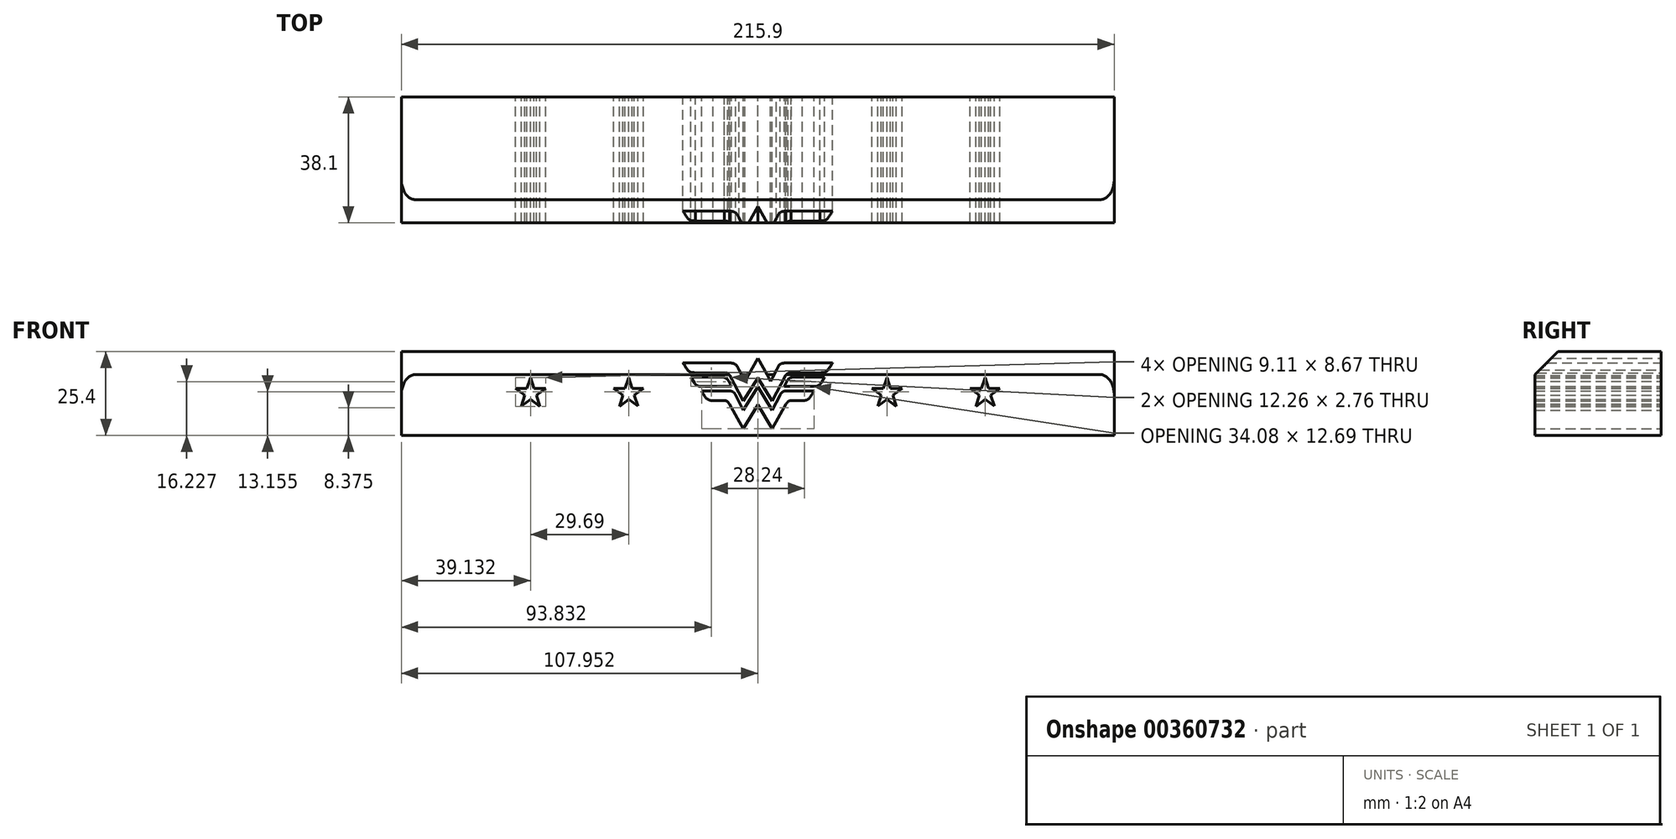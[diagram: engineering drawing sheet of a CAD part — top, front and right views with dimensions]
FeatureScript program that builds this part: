
annotation { "Feature Type Name" : "Feature", "Feature Type Description" : "" }
export const myFeature = defineFeature(function(context is Context, id is Id, definition is map)
    precondition{}
    {
        {
            var Q0;
            Q0=qCreatedBy(makeId("Front.planeOp"),FACE);
            var sketch = newSketch(context, id + "F0", { "sketchPlane" : qUnion([Q0])});
            skLineSegment(sketch, "E0.bottom", {"start": v(-107.29, 21.01) * mm, "end": v(108.61, 21.01) * mm});
            skLineSegment(sketch, "E0.top", {"start": v(-107.29, -4.39) * mm, "end": v(108.61, -4.39) * mm});
            skLineSegment(sketch, "E0.left", {"start": v(-107.29, 21.01) * mm, "end": v(-107.29, -4.39) * mm});
            skLineSegment(sketch, "E0.right", {"start": v(108.61, 21.01) * mm, "end": v(108.61, -4.39) * mm});
            skPoint(sketch, "E1", {"position": v(0.66, 21.01) * mm});
            skLineSegment(sketch, "E2", {"start": v(0.66, 21.01) * mm, "end": v(0.66, -4.39) * mm, "construction": true});
            skPoint(sketch, "E3", {"position": v(-24.74, 21.01) * mm});
            skPoint(sketch, "E4.MirrorP", {"position": v(26.06, 21.01) * mm});
            skLineSegment(sketch, "E5", {"start": v(-24.74, 21.01) * mm, "end": v(-24.74, -4.39) * mm, "construction": true});
            skLineSegment(sketch, "E6", {"start": v(26.06, 21.01) * mm, "end": v(26.06, -4.39) * mm, "construction": true});
            skLineSegment(sketch, "E7", {"start": v(-21.99, 17.6) * mm, "end": v(-8.5, 17.6) * mm});
            skLineSegment(sketch, "E8", {"start": v(-5.01, 15.43) * mm, "end": v(-3.23, 12.05) * mm});
            skLineSegment(sketch, "E9", {"start": v(-3.23, 12.05) * mm, "end": v(0.66, 18.98) * mm});
            skFitSpline(sketch, "E10", {"points": [v(-8.5, 17.6) * mm, v(-5.01, 15.43) * mm], "startDerivative": vector(7.3, -0.1) * mm, "endDerivative": vector(2.43, -5.07) * mm});
            skFitSpline(sketch, "E11", {"points": [v(-21.99, 17.6) * mm, v(-18.2, 14.59) * mm], "startDerivative": vector(5.99, -9.84) * mm, "endDerivative": vector(5.38, -0.2) * mm});
            skLineSegment(sketch, "E12", {"start": v(-18.2, 14.59) * mm, "end": v(-9.4, 14.59) * mm});
            skLineSegment(sketch, "E13", {"start": v(-7.78, 13.77) * mm, "end": v(-3.69, 5.99) * mm});
            skLineSegment(sketch, "E14", {"start": v(-3.69, 5.99) * mm, "end": v(0.66, 13.03) * mm});
            skFitSpline(sketch, "E15", {"points": [v(-9.4, 14.59) * mm, v(-7.78, 13.77) * mm], "startDerivative": vector(2.45, -0.06) * mm, "endDerivative": vector(1.52, -2.05) * mm});
            skLineSegment(sketch, "E16", {"start": v(-19.59, 13.22) * mm, "end": v(-10.08, 13.22) * mm});
            skLineSegment(sketch, "E17", {"start": v(-8.13, 12.02) * mm, "end": v(-7.33, 10.45) * mm});
            skLineSegment(sketch, "E18", {"start": v(-7.33, 10.45) * mm, "end": v(-16.64, 10.45) * mm});
            skLineSegment(sketch, "E19", {"start": v(-18.5, 11.48) * mm, "end": v(-19.59, 13.22) * mm});
            skPoint(sketch, "E20.visualSharp", {"position": v(-17.86, 10.45) * mm});
            skArc(sketch, "E20.filletArc", {"start": v(-18.5, 11.48) * mm, "mid": v(-17.7, 10.73) * mm, "end": v(-16.64, 10.45) * mm});
            skPoint(sketch, "E21.visualSharp", {"position": v(-8.73, 13.22) * mm});
            skArc(sketch, "E21.filletArc", {"start": v(-8.13, 12.02) * mm, "mid": v(-8.93, 12.9) * mm, "end": v(-10.08, 13.22) * mm});
            skLineSegment(sketch, "E22", {"start": v(-16.38, 9.08) * mm, "end": v(-8.11, 9.08) * mm});
            skLineSegment(sketch, "E23", {"start": v(-6.05, 7.77) * mm, "end": v(-3.69, 3.28) * mm});
            skLineSegment(sketch, "E24", {"start": v(-3.69, 3.28) * mm, "end": v(0.66, 10.33) * mm});
            skFitSpline(sketch, "E25", {"points": [v(-16.38, 9.08) * mm, v(-12.85, 6.16) * mm], "startDerivative": vector(4.52, -7.88) * mm, "endDerivative": vector(4.96, -0.07) * mm});
            skLineSegment(sketch, "E26", {"start": v(-12.85, 6.16) * mm, "end": v(-9.48, 6.16) * mm});
            skFitSpline(sketch, "E27", {"points": [v(-9.48, 6.16) * mm, v(-7.94, 5.14) * mm], "startDerivative": vector(2.85, -0.12) * mm, "endDerivative": vector(1.74, -2.2) * mm});
            skLineSegment(sketch, "E28", {"start": v(-7.94, 5.14) * mm, "end": v(-3.69, -2.36) * mm});
            skLineSegment(sketch, "E29", {"start": v(-3.69, -2.36) * mm, "end": v(0.66, 4.88) * mm});
            skLineSegment(sketch, "E30.MirrorCS", {"start": v(4.55, 12.05) * mm, "end": v(0.66, 18.98) * mm});
            skLineSegment(sketch, "E31.MirrorCS", {"start": v(6.33, 15.43) * mm, "end": v(4.55, 12.05) * mm});
            skFitSpline(sketch, "E32.MirrorCS", {"points": [v(9.82, 17.6) * mm, v(6.33, 15.43) * mm], "startDerivative": vector(-7.3, -0.1) * mm, "endDerivative": vector(-2.43, -5.07) * mm});
            skLineSegment(sketch, "E33.MirrorCS", {"start": v(23.31, 17.6) * mm, "end": v(9.82, 17.6) * mm});
            skFitSpline(sketch, "E34.MirrorCS", {"points": [v(23.31, 17.6) * mm, v(19.52, 14.59) * mm], "startDerivative": vector(-5.99, -9.84) * mm, "endDerivative": vector(-5.38, -0.2) * mm});
            skLineSegment(sketch, "E35.MirrorCS", {"start": v(19.52, 14.59) * mm, "end": v(10.73, 14.59) * mm});
            skFitSpline(sketch, "E36.MirrorCS", {"points": [v(10.73, 14.59) * mm, v(9.1, 13.77) * mm], "startDerivative": vector(-2.45, -0.06) * mm, "endDerivative": vector(-1.52, -2.05) * mm});
            skLineSegment(sketch, "E37.MirrorCS", {"start": v(9.1, 13.77) * mm, "end": v(5.01, 5.99) * mm});
            skLineSegment(sketch, "E38.MirrorCS", {"start": v(5.01, 5.99) * mm, "end": v(0.66, 13.03) * mm});
            skLineSegment(sketch, "E39.MirrorCS", {"start": v(20.91, 13.22) * mm, "end": v(11.4, 13.22) * mm});
            skLineSegment(sketch, "E40.MirrorCS", {"start": v(19.82, 11.48) * mm, "end": v(20.91, 13.22) * mm});
            skArc(sketch, "E41.MirrorCS", {"start": v(19.82, 11.48) * mm, "mid": v(19.03, 10.73) * mm, "end": v(17.97, 10.45) * mm});
            skLineSegment(sketch, "E42.MirrorCS", {"start": v(8.65, 10.45) * mm, "end": v(17.97, 10.45) * mm});
            skLineSegment(sketch, "E43.MirrorCS", {"start": v(9.45, 12.02) * mm, "end": v(8.65, 10.45) * mm});
            skArc(sketch, "E44.MirrorCS", {"start": v(9.45, 12.02) * mm, "mid": v(10.26, 12.9) * mm, "end": v(11.4, 13.22) * mm});
            skLineSegment(sketch, "E45.MirrorCS", {"start": v(17.7, 9.08) * mm, "end": v(9.44, 9.08) * mm});
            skLineSegment(sketch, "E46.MirrorCS", {"start": v(7.37, 7.77) * mm, "end": v(5.01, 3.28) * mm});
            skLineSegment(sketch, "E47.MirrorCS", {"start": v(5.01, 3.28) * mm, "end": v(0.66, 10.33) * mm});
            skFitSpline(sketch, "E48.MirrorCS", {"points": [v(17.7, 9.08) * mm, v(14.18, 6.16) * mm], "startDerivative": vector(-4.52, -7.88) * mm, "endDerivative": vector(-4.96, -0.07) * mm});
            skLineSegment(sketch, "E49.MirrorCS", {"start": v(14.18, 6.16) * mm, "end": v(10.8, 6.16) * mm});
            skFitSpline(sketch, "E50.MirrorCS", {"points": [v(10.8, 6.16) * mm, v(9.27, 5.14) * mm], "startDerivative": vector(-2.85, -0.12) * mm, "endDerivative": vector(-1.74, -2.2) * mm});
            skLineSegment(sketch, "E51.MirrorCS", {"start": v(9.27, 5.14) * mm, "end": v(5.01, -2.36) * mm});
            skLineSegment(sketch, "E52.MirrorCS", {"start": v(5.01, -2.36) * mm, "end": v(0.66, 4.88) * mm});
            skFitSpline(sketch, "E53", {"points": [v(-8.11, 9.08) * mm, v(-6.05, 7.77) * mm], "startDerivative": vector(2.51, -0.05) * mm, "endDerivative": vector(1.66, -3.55) * mm});
            skFitSpline(sketch, "E54.MirrorCS", {"points": [v(9.44, 9.08) * mm, v(7.37, 7.77) * mm], "startDerivative": vector(-2.51, -0.05) * mm, "endDerivative": vector(-1.66, -3.55) * mm});
            skSolve(sketch);
        }
        {
            var Q0;
            Q0 = qSketchRegion(id + "F0", true);
            extrude(context, id + "F1", {"entities" : qUnion([Q0]), "depth" : 38.1 * mm, "offsetDistance" : 25.4 * mm});
        }
        {
            var Q0;
            Q0=qCreatedBy(makeId("Front.planeOp"),FACE);
            var sketch = newSketch(context, id + "F2", { "sketchPlane" : qUnion([Q0])});
            skPoint(sketch, "E55.0", {"position": v(0, 0) * mm});
            skPoint(sketch, "E55.1", {"position": v(0.66, 21.01) * mm});
            skPoint(sketch, "E56.0", {"position": v(-107.29, 21.01) * mm});
            skPoint(sketch, "E56.1", {"position": v(108.61, 21.01) * mm});
            skLineSegment(sketch, "E57", {"start": v(-107.29, 21.01) * mm, "end": v(0.66, 21.01) * mm, "construction": true});
            skPoint(sketch, "E58", {"position": v(-53.31, 21.01) * mm});
            skLineSegment(sketch, "E59", {"start": v(0.66, 21.01) * mm, "end": v(108.61, 21.01) * mm, "construction": true});
            skPoint(sketch, "E60", {"position": v(54.64, 21.01) * mm});
            skLineSegment(sketch, "E61", {"start": v(-53.31, 21.01) * mm, "end": v(-53.31, -6.56) * mm, "construction": true});
            skLineSegment(sketch, "E62", {"start": v(54.64, 21.01) * mm, "end": v(54.64, -9.6) * mm, "construction": true});
            skPoint(sketch, "E63.0", {"position": v(-107.29, -4.39) * mm});
            skPoint(sketch, "E63.1", {"position": v(108.61, -4.39) * mm});
            skLineSegment(sketch, "E64", {"start": v(-107.29, 21.01) * mm, "end": v(-107.29, -4.39) * mm, "construction": true});
            skLineSegment(sketch, "E65", {"start": v(108.61, 21.01) * mm, "end": v(108.61, -4.39) * mm, "construction": true});
            skPoint(sketch, "E66", {"position": v(-107.29, 8.31) * mm});
            skPoint(sketch, "E67", {"position": v(108.61, 8.31) * mm});
            skPoint(sketch, "E68.0.midPoint", {"position": v(-34.77, 7.12) * mm});
            skLineSegment(sketch, "E69", {"start": v(-41.27, 4.43) * mm, "end": v(-40.2, 7.74) * mm});
            skLineSegment(sketch, "E70", {"start": v(-38.48, 13.1) * mm, "end": v(-37.4, 9.8) * mm});
            skLineSegment(sketch, "E71", {"start": v(-35.64, 4.44) * mm, "end": v(-38.46, 6.48) * mm});
            skLineSegment(sketch, "E72", {"start": v(-43.02, 9.78) * mm, "end": v(-39.54, 9.79) * mm});
            skLineSegment(sketch, "E73", {"start": v(-33.91, 9.8) * mm, "end": v(-36.72, 7.75) * mm});
            skLineSegment(sketch, "E74.trimOffspring", {"start": v(-36.72, 7.75) * mm, "end": v(-35.64, 4.44) * mm});
            skLineSegment(sketch, "E75.trimOffspring", {"start": v(-37.4, 9.8) * mm, "end": v(-33.91, 9.8) * mm});
            skLineSegment(sketch, "E76.trimOffspring", {"start": v(-39.54, 9.79) * mm, "end": v(-38.48, 13.1) * mm});
            skLineSegment(sketch, "E77.trimOffspring", {"start": v(-40.2, 7.74) * mm, "end": v(-43.02, 9.78) * mm});
            skLineSegment(sketch, "E78.trimOffspring", {"start": v(-38.46, 6.48) * mm, "end": v(-41.27, 4.43) * mm});
            skPoint(sketch, "E68.cCircle.center.orphan", {"position": v(-38.46, 8.31) * mm});
            skLineSegment(sketch, "E79", {"start": v(0.66, 21.01) * mm, "end": v(0.66, -7.13) * mm, "construction": true});
            skLineSegment(sketch, "E80.MirrorCS", {"start": v(38.72, 9.8) * mm, "end": v(35.24, 9.8) * mm});
            skLineSegment(sketch, "E81.MirrorCS", {"start": v(35.24, 9.8) * mm, "end": v(38.05, 7.75) * mm});
            skLineSegment(sketch, "E82.MirrorCS", {"start": v(38.05, 7.75) * mm, "end": v(36.96, 4.44) * mm});
            skLineSegment(sketch, "E83.MirrorCS", {"start": v(36.96, 4.44) * mm, "end": v(39.78, 6.48) * mm});
            skLineSegment(sketch, "E84.MirrorCS", {"start": v(39.78, 6.48) * mm, "end": v(42.6, 4.43) * mm});
            skLineSegment(sketch, "E85.MirrorCS", {"start": v(42.6, 4.43) * mm, "end": v(41.53, 7.74) * mm});
            skLineSegment(sketch, "E86.MirrorCS", {"start": v(41.53, 7.74) * mm, "end": v(44.35, 9.78) * mm});
            skLineSegment(sketch, "E87.MirrorCS", {"start": v(44.35, 9.78) * mm, "end": v(40.87, 9.79) * mm});
            skLineSegment(sketch, "E88.MirrorCS", {"start": v(40.87, 9.79) * mm, "end": v(39.8, 13.1) * mm});
            skLineSegment(sketch, "E89.MirrorCS", {"start": v(39.8, 13.1) * mm, "end": v(38.72, 9.8) * mm});
            skLineSegment(sketch, "E90.MirrorCS", {"start": v(-67.08, 9.79) * mm, "end": v(-68.15, 13.1) * mm});
            skLineSegment(sketch, "E91.MirrorCS", {"start": v(-68.15, 13.1) * mm, "end": v(-69.23, 9.8) * mm});
            skLineSegment(sketch, "E92.MirrorCS", {"start": v(-69.23, 9.8) * mm, "end": v(-72.71, 9.8) * mm});
            skLineSegment(sketch, "E93.MirrorCS", {"start": v(-72.71, 9.8) * mm, "end": v(-69.9, 7.75) * mm});
            skLineSegment(sketch, "E94.MirrorCS", {"start": v(-69.9, 7.75) * mm, "end": v(-70.99, 4.44) * mm});
            skLineSegment(sketch, "E95.MirrorCS", {"start": v(-70.99, 4.44) * mm, "end": v(-68.17, 6.48) * mm});
            skLineSegment(sketch, "E96.MirrorCS", {"start": v(-68.17, 6.48) * mm, "end": v(-65.36, 4.43) * mm});
            skLineSegment(sketch, "E97.MirrorCS", {"start": v(-65.36, 4.43) * mm, "end": v(-66.42, 7.74) * mm});
            skLineSegment(sketch, "E98.MirrorCS", {"start": v(-66.42, 7.74) * mm, "end": v(-63.6, 9.78) * mm});
            skLineSegment(sketch, "E99.MirrorCS", {"start": v(-63.6, 9.78) * mm, "end": v(-67.08, 9.79) * mm});
            skLineSegment(sketch, "E100.MirrorCS", {"start": v(69.47, 13.1) * mm, "end": v(70.56, 9.8) * mm});
            skLineSegment(sketch, "E101.MirrorCS", {"start": v(68.4, 9.79) * mm, "end": v(69.47, 13.1) * mm});
            skLineSegment(sketch, "E102.MirrorCS", {"start": v(64.93, 9.78) * mm, "end": v(68.4, 9.79) * mm});
            skLineSegment(sketch, "E103.MirrorCS", {"start": v(67.75, 7.74) * mm, "end": v(64.93, 9.78) * mm});
            skLineSegment(sketch, "E104.MirrorCS", {"start": v(66.68, 4.43) * mm, "end": v(67.75, 7.74) * mm});
            skLineSegment(sketch, "E105.MirrorCS", {"start": v(69.5, 6.48) * mm, "end": v(66.68, 4.43) * mm});
            skLineSegment(sketch, "E106.MirrorCS", {"start": v(72.31, 4.44) * mm, "end": v(69.5, 6.48) * mm});
            skLineSegment(sketch, "E107.MirrorCS", {"start": v(71.23, 7.75) * mm, "end": v(72.31, 4.44) * mm});
            skLineSegment(sketch, "E108.MirrorCS", {"start": v(74.04, 9.8) * mm, "end": v(71.23, 7.75) * mm});
            skLineSegment(sketch, "E109.MirrorCS", {"start": v(70.56, 9.8) * mm, "end": v(74.04, 9.8) * mm});
            skSolve(sketch);
        }
        {
            var Q0;
            Q0 = qSketchRegion(id + "F2", true);
            extrude(context, id + "F3", {"entities" : qUnion([Q0]), "operationType" : NewBodyOperationType.REMOVE, "endBound" : BoundingType.UP_TO_NEXT, "depth" : 25.4 * mm, "offsetDistance" : 25.4 * mm});
        }
        {
            var Q0;
            Q0=makeQuery(id+"F1.opExtrude","CAP_EDGE",EDGE,{"disambiguationData":[OSD([sQuery(id+"F0.wireOp",EDGE,"E0.bottom")])],"isStart":false});
            chamfer(context, id + "F4", {"entities" : qUnion([Q0]), "width" : 7 * mm, "tangentPropagation" : true});
        }
        {
            var Q0;
            Q0=makeQuery(id+"F4.opChamfer","BLEND_EDGE",EDGE,{"blendedFrom":[makeQuery(id+"F1.opExtrude","CAP_EDGE",EDGE,{"disambiguationData":[OSD([sQuery(id+"F0.wireOp",EDGE,"E0.bottom")])],"isStart":false}),makeQuery(id+"F1.opExtrude","SWEPT_FACE",FACE,{"disambiguationData":[OSD([sQuery(id+"F0.wireOp",EDGE,"E0.right")])]})],"blendedInto":[makeQuery(id+"F1.opExtrude","SWEPT_FACE",FACE,{"disambiguationData":[OSD([sQuery(id+"F0.wireOp",EDGE,"E0.right")])]})]});
            var Q1;
            Q1=makeQuery(id+"F4.opChamfer","BLEND_EDGE",EDGE,{"blendedFrom":[makeQuery(id+"F1.opExtrude","CAP_EDGE",EDGE,{"disambiguationData":[OSD([sQuery(id+"F0.wireOp",EDGE,"E0.bottom")])],"isStart":false}),makeQuery(id+"F1.opExtrude","SWEPT_FACE",FACE,{"disambiguationData":[OSD([sQuery(id+"F0.wireOp",EDGE,"E0.left")])]})],"blendedInto":[makeQuery(id+"F1.opExtrude","SWEPT_FACE",FACE,{"disambiguationData":[OSD([sQuery(id+"F0.wireOp",EDGE,"E0.left")])]})]});
            fillet(context, id + "F5", {"entities" : qUnion([Q0, Q1]), "tangentPropagation" : true, "radius" : 4.3 * mm, "defaultsChanged" : true, "vertexSettings" : [], "allowEdgeOverflow" : false});
        }
    });
